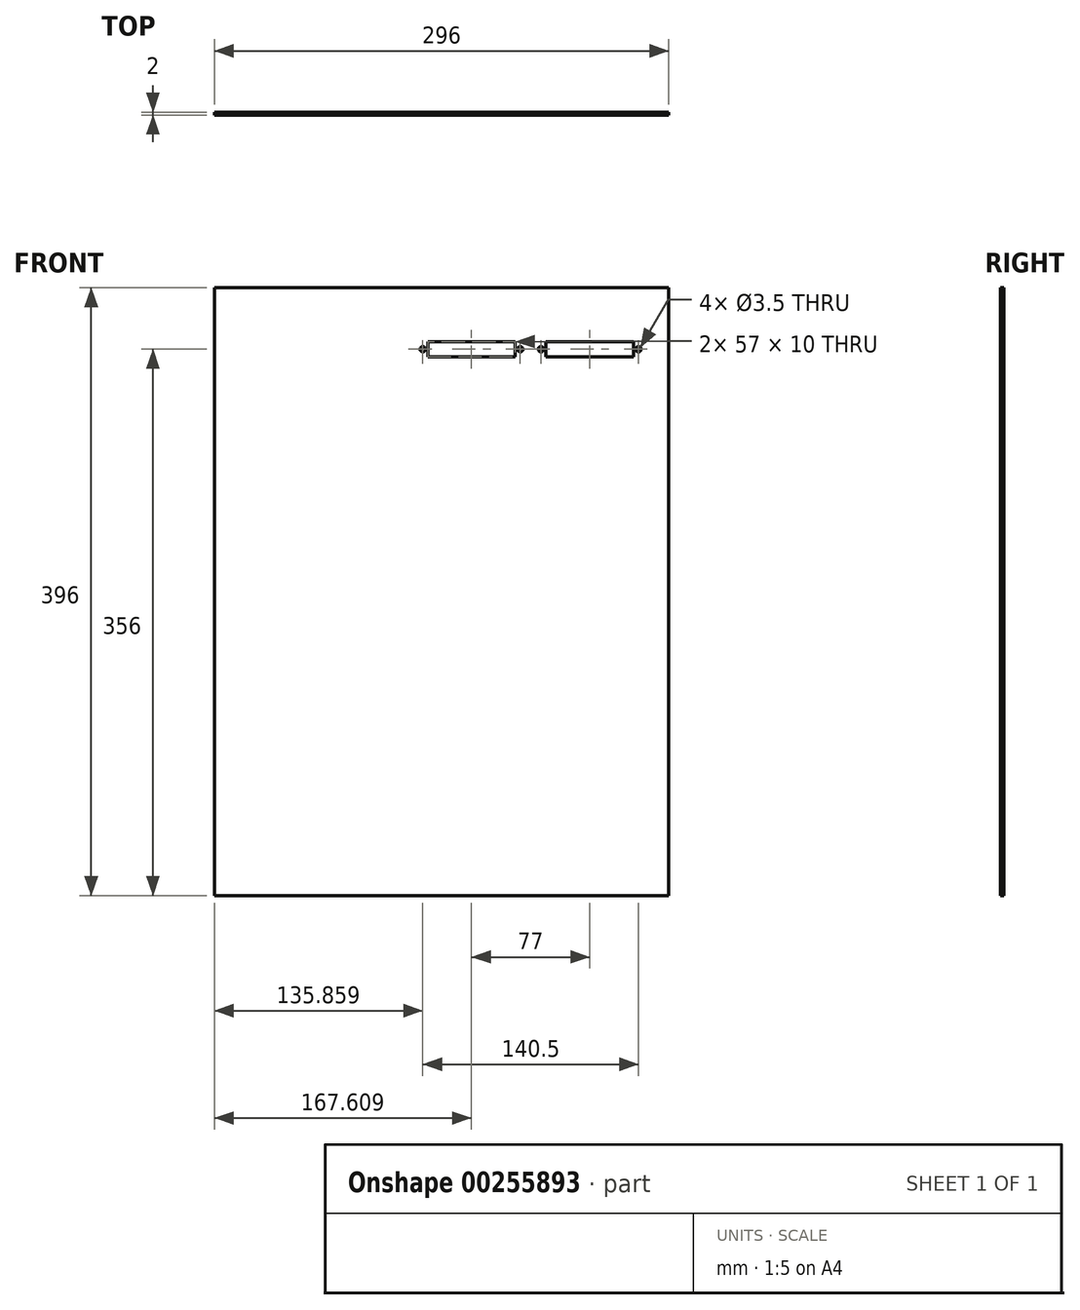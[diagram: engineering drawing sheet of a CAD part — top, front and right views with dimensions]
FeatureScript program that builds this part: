
annotation { "Feature Type Name" : "Feature", "Feature Type Description" : "" }
export const myFeature = defineFeature(function(context is Context, id is Id, definition is map)
    precondition{}
    {
        {
            var Q0;
            Q0=qCreatedBy(makeId("Front.planeOp"),FACE);
            var sketch = newSketch(context, id + "F0", { "sketchPlane" : qUnion([Q0])});
            skLineSegment(sketch, "E0.bottom", {"start": v(148, 198) * mm, "end": v(-148, 198) * mm});
            skLineSegment(sketch, "E0.top", {"start": v(148, -198) * mm, "end": v(-148, -198) * mm});
            skLineSegment(sketch, "E0.left", {"start": v(148, 198) * mm, "end": v(148, -198) * mm});
            skLineSegment(sketch, "E0.right", {"start": v(-148, 198) * mm, "end": v(-148, -198) * mm});
            skPoint(sketch, "E0.middle", {"position": v(0, 0) * mm});
            skLineSegment(sketch, "E1", {"start": v(-148, 158) * mm, "end": v(148, 158) * mm, "construction": true});
            skLineSegment(sketch, "E2.bottom", {"start": v(68.1, 163) * mm, "end": v(125.1, 163) * mm});
            skLineSegment(sketch, "E2.top", {"start": v(68.1, 153) * mm, "end": v(125.1, 153) * mm});
            skLineSegment(sketch, "E2.left", {"start": v(68.1, 163) * mm, "end": v(68.1, 153) * mm});
            skLineSegment(sketch, "E2.right", {"start": v(125.1, 163) * mm, "end": v(125.1, 153) * mm});
            skPoint(sketch, "E2.middle", {"position": v(96.6, 158) * mm});
            skLineSegment(sketch, "E3.bottom", {"start": v(-8.9, 163) * mm, "end": v(48.1, 163) * mm});
            skLineSegment(sketch, "E3.top", {"start": v(-8.9, 153) * mm, "end": v(48.1, 153) * mm});
            skLineSegment(sketch, "E3.left", {"start": v(-8.9, 163) * mm, "end": v(-8.9, 153) * mm});
            skLineSegment(sketch, "E3.right", {"start": v(48.1, 163) * mm, "end": v(48.1, 153) * mm});
            skCircle(sketch, "E4", {"center": v(51.36, 158) * mm, "radius": 1.75 * mm});
            skCircle(sketch, "E5", {"center": v(64.86, 158) * mm, "radius": 1.75 * mm});
            skCircle(sketch, "E6", {"center": v(128.36, 158) * mm, "radius": 1.75 * mm});
            skCircle(sketch, "E7", {"center": v(-12.14, 158) * mm, "radius": 1.75 * mm});
            skPoint(sketch, "E8", {"position": v(19.6, 158) * mm});
            skLineSegment(sketch, "E9", {"start": v(-8.9, 163) * mm, "end": v(48.1, 153) * mm, "construction": true});
            skLineSegment(sketch, "E10", {"start": v(68.1, 163) * mm, "end": v(125.1, 153) * mm, "construction": true});
            skSolve(sketch);
        }
        {
            var Q0;
            Q0=makeQuery(id+"F0.imprint","IMPRINT",FACE,{"disambiguationData":[TD([[makeQuery(id+"F0.imprint","IMPRINT",EDGE,{"derivedFrom":sQuery(id+"F0.wireOp",EDGE,"E0.bottom")}),1.0]])]});
            extrude(context, id + "F1", {"entities" : qUnion([Q0]), "depth" : 2 * mm});
        }
    });
